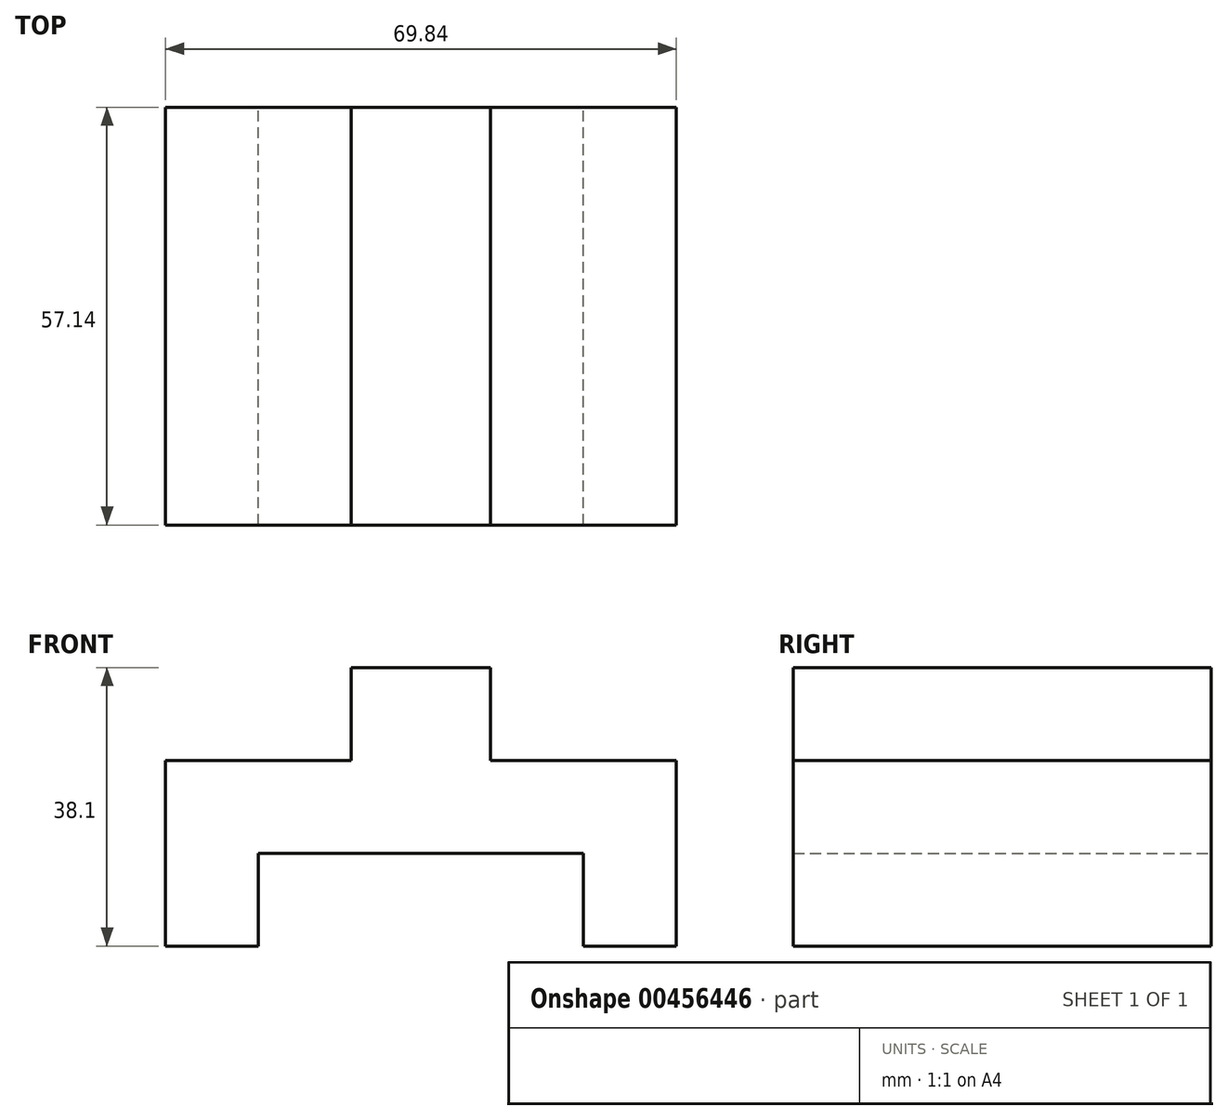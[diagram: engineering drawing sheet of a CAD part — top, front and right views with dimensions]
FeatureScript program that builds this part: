
annotation { "Feature Type Name" : "Feature", "Feature Type Description" : "" }
export const myFeature = defineFeature(function(context is Context, id is Id, definition is map)
    precondition{}
    {
        {
            var Q0;
            Q0=qCreatedBy(makeId("Front.planeOp"),FACE);
            var sketch = newSketch(context, id + "F0", { "sketchPlane" : qUnion([Q0])});
            skLineSegment(sketch, "E0.bottom", {"start": v(-9.53, 19.05) * mm, "end": v(9.53, 19.05) * mm});
            skLineSegment(sketch, "E0.top", {"start": v(-34.93, -19.05) * mm, "end": v(-22.23, -19.05) * mm});
            skLineSegment(sketch, "E0.left", {"start": v(-34.93, 6.35) * mm, "end": v(-34.93, -19.05) * mm});
            skLineSegment(sketch, "E0.right", {"start": v(34.93, 6.35) * mm, "end": v(34.93, -19.05) * mm});
            skPoint(sketch, "E0.middle", {"position": v(0, 0) * mm});
            skLineSegment(sketch, "E1.top", {"start": v(-34.93, 6.35) * mm, "end": v(-9.53, 6.35) * mm});
            skLineSegment(sketch, "E1.right", {"start": v(-9.53, 19.05) * mm, "end": v(-9.53, 6.35) * mm});
            skLineSegment(sketch, "E2.MirrorCS", {"start": v(34.93, 6.35) * mm, "end": v(9.53, 6.35) * mm});
            skLineSegment(sketch, "E3.MirrorCS", {"start": v(9.53, 19.05) * mm, "end": v(9.53, 6.35) * mm});
            skLineSegment(sketch, "E4.top", {"start": v(-22.23, -6.35) * mm, "end": v(22.22, -6.35) * mm});
            skLineSegment(sketch, "E4.left", {"start": v(-22.23, -19.05) * mm, "end": v(-22.23, -6.35) * mm});
            skLineSegment(sketch, "E4.right", {"start": v(22.22, -19.05) * mm, "end": v(22.22, -6.35) * mm});
            skLineSegment(sketch, "E5.trimOffspring", {"start": v(22.22, -19.05) * mm, "end": v(34.93, -19.05) * mm});
            skPoint(sketch, "E6.orphan", {"position": v(34.93, 19.05) * mm});
            skPoint(sketch, "E7.orphan", {"position": v(-34.93, 19.05) * mm});
            skSolve(sketch);
        }
        {
            var Q0;
            Q0=makeQuery(id+"F0.imprint","IMPRINT",FACE,{"disambiguationData":[TD([[makeQuery(id+"F0.imprint","IMPRINT",EDGE,{"derivedFrom":sQuery(id+"F0.wireOp",EDGE,"E0.bottom")}),-1.0]])]});
            extrude(context, id + "F1", {"entities" : qUnion([Q0]), "endBound" : BoundingType.SYMMETRIC, "depth" : 57.15 * mm});
        }
    });
